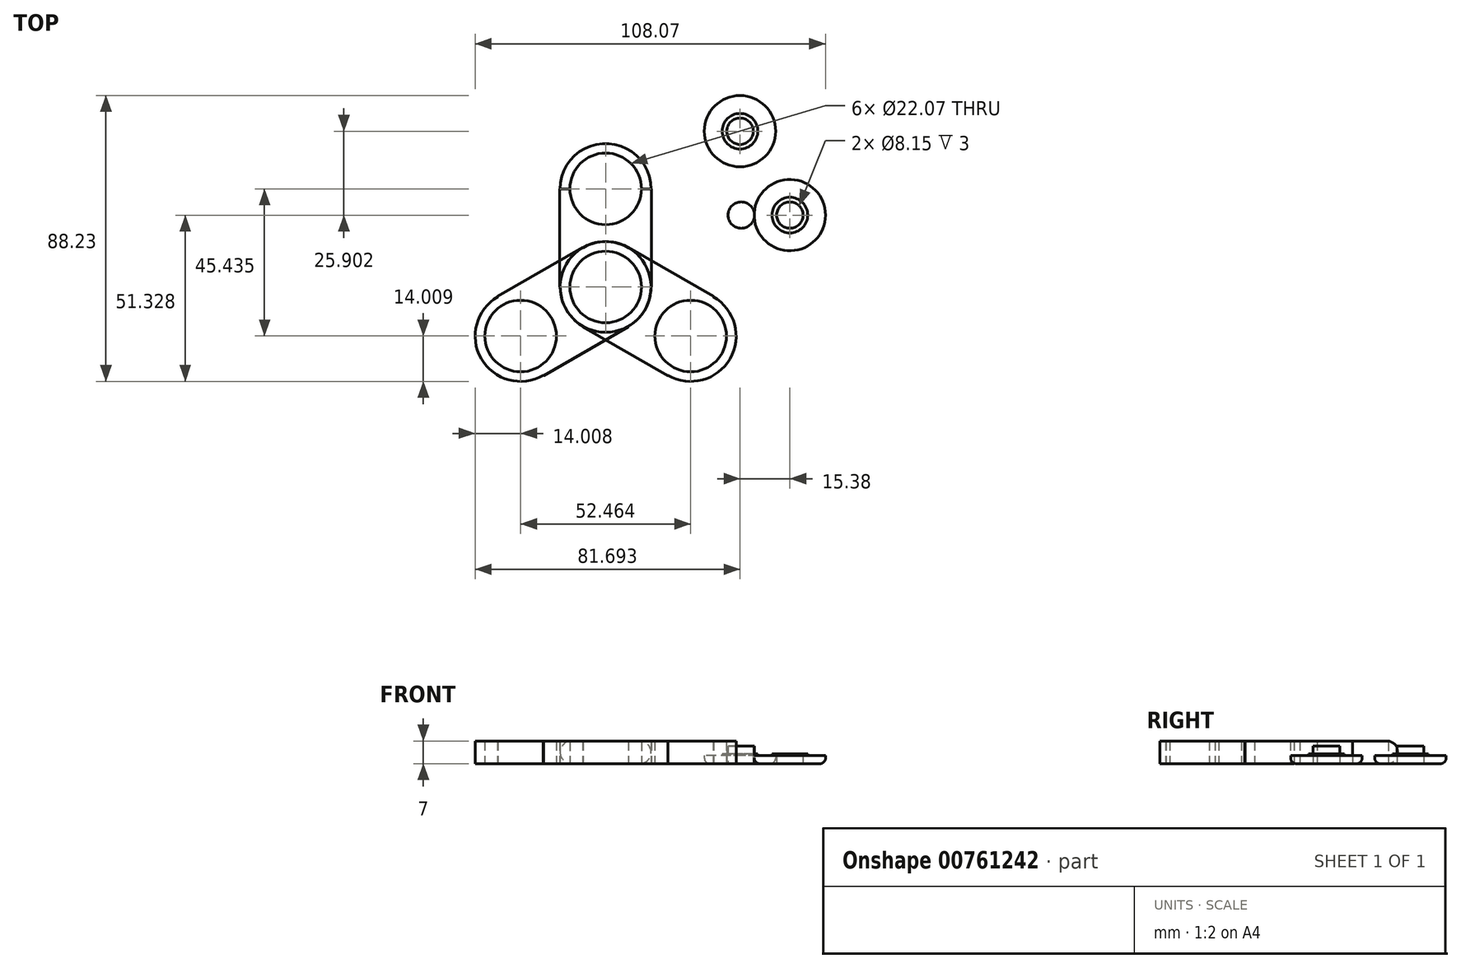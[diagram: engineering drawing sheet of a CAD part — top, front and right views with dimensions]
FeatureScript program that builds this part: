
annotation { "Feature Type Name" : "Feature", "Feature Type Description" : "" }
export const myFeature = defineFeature(function(context is Context, id is Id, definition is map)
    precondition{}
    {
        {
            var Q0;
            Q0=qCreatedBy(makeId("Top.planeOp"),FACE);
            var sketch = newSketch(context, id + "F0", { "sketchPlane" : qUnion([Q0])});
            skLineSegment(sketch, "E0.0", {"start": v(14.14, 16.08) * mm, "end": v(14.14, -14.2) * mm});
            skLineSegment(sketch, "E0.1", {"start": v(14.14, -14.2) * mm, "end": v(-14.14, -14.2) * mm});
            skLineSegment(sketch, "E0.2", {"start": v(-14.14, -14.2) * mm, "end": v(-14.14, 16.08) * mm});
            skLineSegment(sketch, "E0.3", {"start": v(-14.14, 16.08) * mm, "end": v(14.14, 16.08) * mm});
            skPoint(sketch, "E0.0.midPoint", {"position": v(14.14, 0.94) * mm});
            skCircle(sketch, "E1", {"center": v(0, 16.08) * mm, "radius": 14.01 * mm});
            skCircle(sketch, "E2", {"center": v(0, 16.08) * mm, "radius": 11.04 * mm});
            skCircle(sketch, "E3", {"center": v(0, -14.2) * mm, "radius": 14.01 * mm});
            skCircle(sketch, "E4", {"center": v(0, -14.2) * mm, "radius": 11.04 * mm});
            skSolve(sketch);
        }
        {
            var Q0;
            Q0=qCreatedBy(makeId("Top.planeOp"),FACE);
            var sketch = newSketch(context, id + "F1", { "sketchPlane" : qUnion([Q0])});
            skCircle(sketch, "E5", {"center": v(41.45, 33.87) * mm, "radius": 11 * mm});
            skCircle(sketch, "E6", {"center": v(41.45, 33.87) * mm, "radius": 5.5 * mm});
            skCircle(sketch, "E7", {"center": v(41.45, 33.87) * mm, "radius": 4.08 * mm});
            skCircle(sketch, "E8", {"center": v(41.83, 7.97) * mm, "radius": 11 * mm});
            skCircle(sketch, "E9", {"center": v(41.83, 7.97) * mm, "radius": 5.5 * mm});
            skCircle(sketch, "E10", {"center": v(41.83, 7.97) * mm, "radius": 4.08 * mm});
            skSolve(sketch);
        }
        {
            var Q0;
            {var subQ0=sQuery(id+"F0.wireOp",EDGE,"E3");var subQ1=sQuery(id+"F0.wireOp",EDGE,"E0.1");var subQ2=makeQuery(id+"F0.imprint","INTERSECT",VERTEX,{"disambiguationData":[OD(0.0)],"derivedFrom":[subQ1,subQ0]});Q0=makeQuery(id+"F0.imprint","IMPRINT",FACE,{"disambiguationData":[TD([[makeQuery(id+"F0.imprint","IMPRINT",EDGE,{"disambiguationData":[TD([[subQ2,-1.0]])],"derivedFrom":subQ1}),1.0]])]});}
            var Q1;
            {var subQ0=sQuery(id+"F0.wireOp",EDGE,"E3");var subQ1=sQuery(id+"F0.wireOp",EDGE,"E0.1");var subQ2=makeQuery(id+"F0.imprint","INTERSECT",VERTEX,{"disambiguationData":[OD(0.0)],"derivedFrom":[subQ1,subQ0]});Q1=makeQuery(id+"F0.imprint","IMPRINT",FACE,{"disambiguationData":[TD([[makeQuery(id+"F0.imprint","IMPRINT",EDGE,{"disambiguationData":[TD([[subQ2,-1.0]])],"derivedFrom":subQ1}),-1.0]])]});}
            var Q2;
            {var subQ2=sQuery(id+"F0.wireOp",EDGE,"E0.0");Q2=makeQuery(id+"F0.imprint","IMPRINT",FACE,{"disambiguationData":[TD([[makeQuery(id+"F0.imprint","IMPRINT",EDGE,{"derivedFrom":subQ2}),-1.0]])]});}
            var Q3;
            {var subQ0=sQuery(id+"F0.wireOp",EDGE,"E1");var subQ1=sQuery(id+"F0.wireOp",EDGE,"E0.3");var subQ2=makeQuery(id+"F0.imprint","INTERSECT",VERTEX,{"disambiguationData":[OD(0.0)],"derivedFrom":[subQ1,subQ0]});Q3=makeQuery(id+"F0.imprint","IMPRINT",FACE,{"disambiguationData":[TD([[makeQuery(id+"F0.imprint","IMPRINT",EDGE,{"disambiguationData":[TD([[subQ2,-1.0]])],"derivedFrom":subQ1}),-1.0]])]});}
            var Q4;
            {var subQ0=sQuery(id+"F0.wireOp",EDGE,"E1");var subQ1=sQuery(id+"F0.wireOp",EDGE,"E0.3");var subQ2=makeQuery(id+"F0.imprint","INTERSECT",VERTEX,{"disambiguationData":[OD(0.0)],"derivedFrom":[subQ1,subQ0]});Q4=makeQuery(id+"F0.imprint","IMPRINT",FACE,{"disambiguationData":[TD([[makeQuery(id+"F0.imprint","IMPRINT",EDGE,{"disambiguationData":[TD([[subQ2,-1.0]])],"derivedFrom":subQ1}),1.0]])]});}
            extrude(context, id + "F2", {"entities" : qUnion([Q0, Q1, Q2, Q3, Q4]), "depth" : 7 * mm, "offsetDistance" : 25 * mm});
        }
        {
            var Q0;
            Q0=makeQuery(id+"F1.imprint","IMPRINT",FACE,{"disambiguationData":[TD([[makeQuery(id+"F1.imprint","IMPRINT",EDGE,{"derivedFrom":sQuery(id+"F1.wireOp",EDGE,"E5")}),1.0]])]});
            var Q1;
            Q1=makeQuery(id+"F1.imprint","IMPRINT",FACE,{"disambiguationData":[TD([[makeQuery(id+"F1.imprint","IMPRINT",EDGE,{"derivedFrom":sQuery(id+"F1.wireOp",EDGE,"E8")}),1.0]])]});
            extrude(context, id + "F3", {"entities" : qUnion([Q0, Q1]), "depth" : 2.5 * mm, "offsetDistance" : 25 * mm});
        }
        {
            var Q0;
            Q0=makeQuery(id+"F1.imprint","IMPRINT",FACE,{"disambiguationData":[TD([[makeQuery(id+"F1.imprint","IMPRINT",EDGE,{"derivedFrom":sQuery(id+"F1.wireOp",EDGE,"E6")}),1.0]])]});
            extrude(context, id + "F4", {"entities" : qUnion([Q0]), "operationType" : NewBodyOperationType.ADD, "depth" : 3 * mm, "offsetDistance" : 25 * mm});
        }
        {
            var Q0;
            Q0=makeQuery(id+"F1.imprint","IMPRINT",FACE,{"disambiguationData":[TD([[makeQuery(id+"F1.imprint","IMPRINT",EDGE,{"derivedFrom":sQuery(id+"F1.wireOp",EDGE,"E9")}),1.0]])]});
            extrude(context, id + "F5", {"entities" : qUnion([Q0]), "operationType" : NewBodyOperationType.ADD, "depth" : 3 * mm, "offsetDistance" : 25 * mm});
        }
        {
            var Q0;
            Q0=makeQuery(id+"F1.imprint","IMPRINT",FACE,{"disambiguationData":[TD([[makeQuery(id+"F1.imprint","IMPRINT",EDGE,{"derivedFrom":sQuery(id+"F1.wireOp",EDGE,"E10")}),1.0]])]});
            var Q1;
            Q1=makeQuery(id+"F1.imprint","IMPRINT",FACE,{"disambiguationData":[TD([[makeQuery(id+"F1.imprint","IMPRINT",EDGE,{"derivedFrom":sQuery(id+"F1.wireOp",EDGE,"E7")}),1.0]])]});
            extrude(context, id + "F6", {"entities" : qUnion([Q0, Q1]), "depth" : 5.5 * mm, "offsetDistance" : 25 * mm});
        }
        {
            var Q0;
            Q0=makeQuery(id+"F3.opExtrude","CAP_EDGE",EDGE,{"disambiguationData":[OSD([sQuery(id+"F1.wireOp",EDGE,"E5")])],"isStart":true});
            var Q1;
            Q1=makeQuery(id+"F3.opExtrude","CAP_EDGE",EDGE,{"disambiguationData":[OSD([sQuery(id+"F1.wireOp",EDGE,"E8")])],"isStart":true});
            fillet(context, id + "F7", {"entities" : qUnion([Q0, Q1]), "radius" : 1.75 * mm, "tangentPropagation" : true, "allowEdgeOverflow" : false});
        }
        {
            var Q0;
            Q0=makeQuery(id+"F3.opExtrude","SWEPT_BODY",BODY,{"disambiguationData":[OSD([sQuery(id+"F1.wireOp",EDGE,"E8"),sQuery(id+"F1.wireOp",EDGE,"E9")])]});
            transform(context, id + "F8", {"entities" : qUnion([Q0]), "transformType" : TransformType.TRANSLATION_3D, "dx" : 15 * mm, "dy" : 0 * mm, "dz" : 0 * mm, "makeCopy" : true});
        }
        {
            var Q0;
            Q0=makeQuery(id+"F3.opExtrude","SWEPT_BODY",BODY,{"disambiguationData":[OSD([sQuery(id+"F1.wireOp",EDGE,"E8"),sQuery(id+"F1.wireOp",EDGE,"E9")])]});
            deleteBodies(context, id + "F9", {"entities" : qUnion([Q0])});
        }
        {
            var Q0;
            Q0=makeQuery(id+"F2.opExtrude","SWEPT_BODY",BODY,{"disambiguationData":[OSD([sQuery(id+"F0.wireOp",EDGE,"E0.0"),sQuery(id+"F0.wireOp",EDGE,"E0.1"),sQuery(id+"F0.wireOp",EDGE,"E0.2"),sQuery(id+"F0.wireOp",EDGE,"E0.3"),sQuery(id+"F0.wireOp",EDGE,"E1"),sQuery(id+"F0.wireOp",EDGE,"E2"),sQuery(id+"F0.wireOp",EDGE,"E3"),sQuery(id+"F0.wireOp",EDGE,"E4")])]});
            var Q1;
            Q1=makeQuery(id+"F2.opExtrude","CAP_EDGE",EDGE,{"disambiguationData":[OSD([sQuery(id+"F0.wireOp",EDGE,"E4")])],"isStart":false});
            circularPattern(context, id + "F10", {"entities" : qUnion([Q0]), "axis" : qUnion([Q1]), "angle" : 360 * degree, "instanceCount" : 3, "equalSpace" : true});
        }
        {
            var Q0;
            Q0=makeQuery(id+"F2.opExtrude","CAP_EDGE",EDGE,{"disambiguationData":[OSD([sQuery(id+"F0.wireOp",EDGE,"E1")])],"isStart":false});
            var Q1;
            Q1=makeQuery(id+"F2.opExtrude","CAP_EDGE",EDGE,{"disambiguationData":[OSD([sQuery(id+"F0.wireOp",EDGE,"E1")])],"isStart":true});
            fillet(context, id + "F11", {"entities" : qUnion([Q0, Q1]), "tangentPropagation" : true, "radius" : 3.5 * mm, "defaultsChanged" : true, "vertexSettings" : [], "allowEdgeOverflow" : false});
        }
    });
